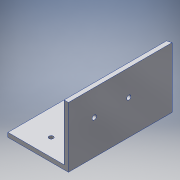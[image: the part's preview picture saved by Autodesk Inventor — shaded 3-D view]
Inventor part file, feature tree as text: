
AUTODESK INVENTOR PART (.ipt)
format: ipt  version: 2016 (Build 200138000, 138)  size: 120,832 bytes
history: native  units: in
note: dims shown in document units (in); Inventor stores cm internally (conversion verified against a paired STEP export)
features: sketch x3, hole x2, extrude x1, plane x1, split x1
ambient origin geometry x8: Origin, YZ Plane, XZ Plane, XY Plane, X Axis, Y Axis, Z Axis, Center Point
bodies: Solid1 (feature_tree)
feature tree (8):
  extrude  "Extrusion1"  Depth=1.75in
  plane  "Work Plane1"
  split  "Split1"
  hole  "Hole1"  [1 undecoded]
  hole  "Hole2"  [1 undecoded]
  sketch  "Sketch1"  dims[d0=1.75in d1=1.75in]
  sketch  "Sketch2"  dims[d2=0.125in d3=3.0in d4=0.0in]
  sketch  "Sketch3"  dims[d5=15.0deg d6=0.5in d7=1.0in d8=0.125in d9=0.75in d10=0.375in d11=0.25in d12=0.5635in d13=1.0in d14=0.8108in d15=0.75in d16=1.0in d17=0.125in d18=0.75in d19=0.375in d20=0.25in d21=0.5635in d22=1.0in d23=0.8108in d26=0.75in d27=0.75in d28=0.75in d29=0.75in]
note: 2 required parameter values undecoded (feature->parameter linkage not recoverable at this tier; creation-order binding heuristic only, values carry confidence <= 0.55)
